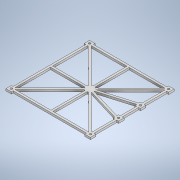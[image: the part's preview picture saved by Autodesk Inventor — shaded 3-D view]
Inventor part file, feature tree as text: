
AUTODESK INVENTOR PART (.ipt)
format: ipt  version: 2020 (Build 240168000, 168)  size: 263,680 bytes
history: native  units: in
note: dims shown in document units (in); Inventor stores cm internally (conversion verified against a paired STEP export)
features: extrude x1, sketch x1
ambient origin geometry x8: Origin, YZ Plane, XZ Plane, XY Plane, X Axis, Y Axis, Z Axis, Center Point
bodies: Solid1 (feature_tree)
feature tree (2):
  extrude  "Extrusion1"  Depth=0.1181in
  sketch  "Sketch1"  dims[d0=5.9055in d1=5.1181in d2=0.5114in d3=0.0157in d4=0.1575in d5=0.315in d6=0.315in d7=0.315in d8=0.315in d9=0.4724in d10=0.122in d11=0.122in d13=0.4724in d14=0.1181in d15=0.1181in d16=0.1181in d17=0.1181in d18=0.1181in d19=0.1181in d20=0.1181in d21=0.1181in d22=0.1181in d23=0.1181in d24=0.1181in d25=0.1181in d26=0.1181in d27=0.0in]
